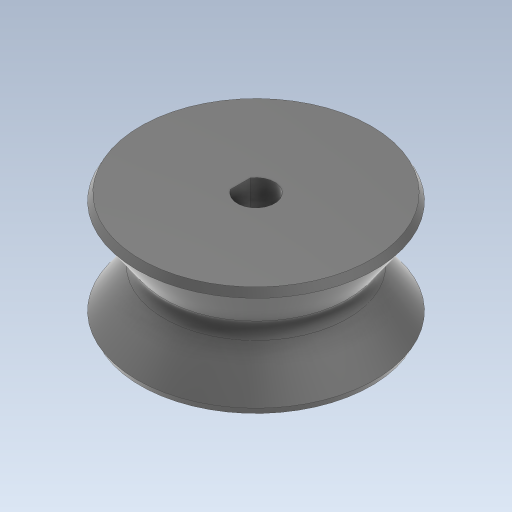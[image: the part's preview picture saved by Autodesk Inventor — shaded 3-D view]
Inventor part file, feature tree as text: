
AUTODESK INVENTOR PART (.ipt)
format: ipt  version: 2023 (Build 270158000, 158)  size: 406,528 bytes
history: native  units: mm
features: chamfer x3, plane x2, sketch x1, revolve x1, extrude x1, fillet x1, hole x1
ambient origin geometry x8: Origin, YZ Plane, XZ Plane, XY Plane, X Axis, Y Axis, Z Axis, Center Point
bodies: Solid1 (feature_tree)
feature tree (10):
  sketch  "Sketch1"  dims[d1=4.7mm d4=15.0mm d5=14.0mm d6=14.0mm d7=90.0deg d8=0.0mm d9=0.0mm d10=1.2mm d11=2.0mm d12=45.0deg d15=30.0deg d20=3.490659mm d71=-12.0mm d92=2.55mm d93=10.0mm d95=2.0mm d98=1.0mm d99=2.0mm d100=45.0deg d102=9.599311mm d103=10.0mm d105=6.5mm d106=6.0mm d107=6.0mm d108=2.0mm d109=90.0deg d110=5.3mm d111=0.0mm d112=0.2mm d113=2.0mm d114=45.0deg]
  revolve  "Revolution1"  [1 undecoded]
  extrude  "Extrusion1"  Depth=5.3mm
  chamfer  "Chamfer1"  Distance=14.0mm
  plane  "Work Plane3"
  plane  "Work Plane4"
  fillet  "Fillet1"  [1 undecoded]
  chamfer  "Chamfer2"  [1 undecoded]
  hole  "Hole4"  [1 undecoded]
  chamfer  "Chamfer3"  Distance=3.490659mm Angle=30.0deg
note: 4 required parameter values undecoded (feature->parameter linkage not recoverable at this tier; creation-order binding heuristic only, values carry confidence <= 0.55)